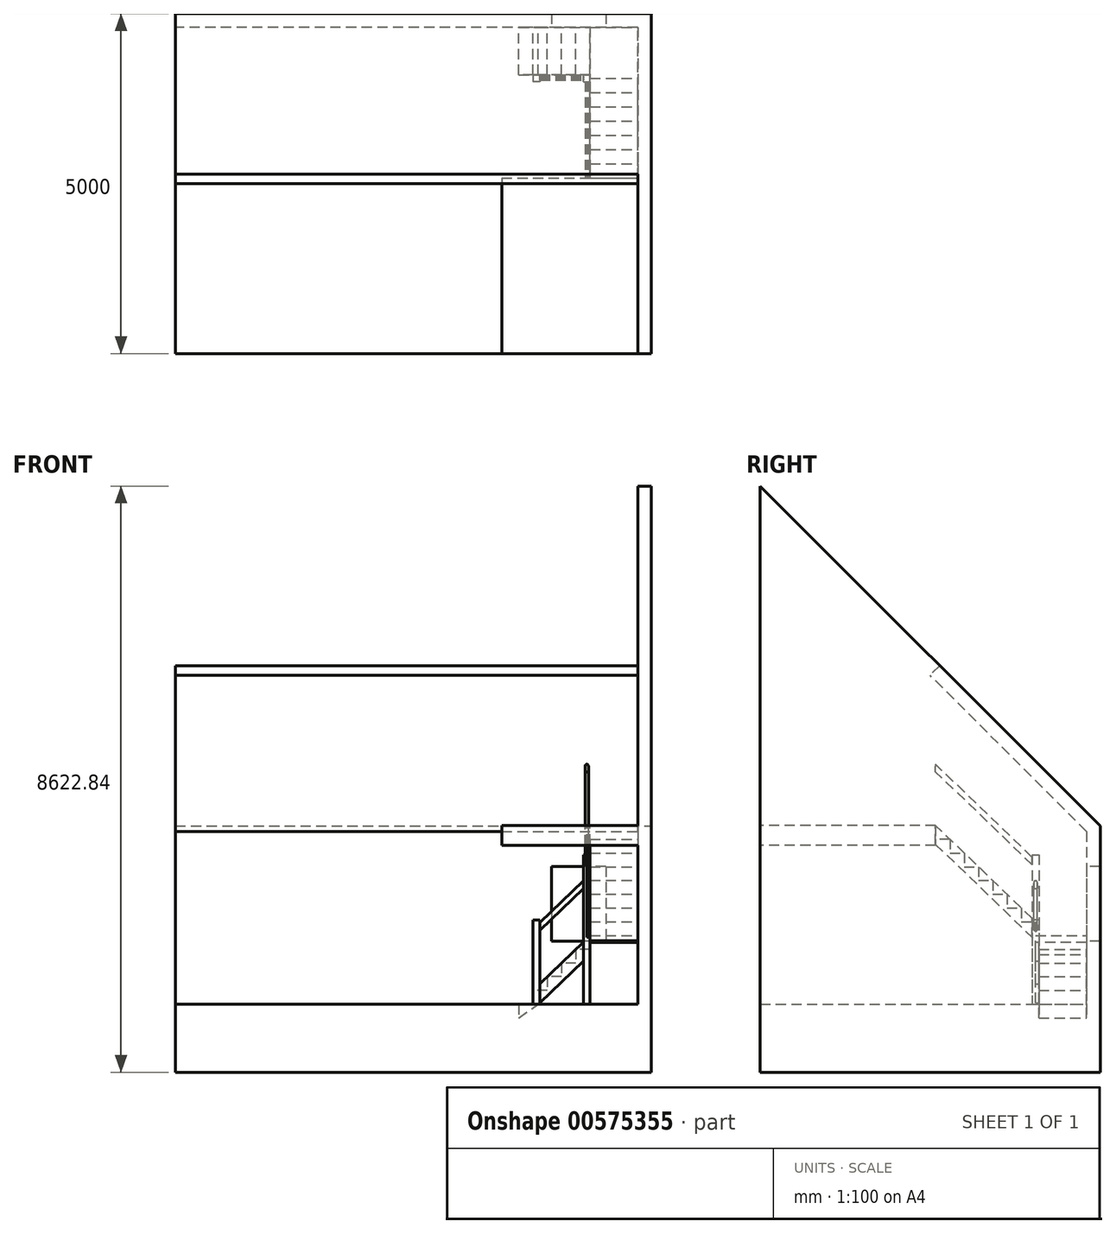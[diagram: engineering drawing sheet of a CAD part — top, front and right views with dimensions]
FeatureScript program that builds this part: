
annotation { "Feature Type Name" : "Feature", "Feature Type Description" : "" }
export const myFeature = defineFeature(function(context is Context, id is Id, definition is map)
    precondition{}
    {
        {
            var Q0;
            Q0=qCreatedBy(makeId("Top.planeOp"),FACE);
            var sketch = newSketch(context, id + "F0", { "sketchPlane" : qUnion([Q0])});
            skLineSegment(sketch, "E0.bottom", {"start": v(-3500, 2500) * mm, "end": v(3500, 2500) * mm});
            skLineSegment(sketch, "E0.top", {"start": v(-3500, -2500) * mm, "end": v(3500, -2500) * mm});
            skLineSegment(sketch, "E0.left", {"start": v(-3500, 2500) * mm, "end": v(-3500, -2500) * mm});
            skLineSegment(sketch, "E0.right", {"start": v(3500, 2500) * mm, "end": v(3500, -2500) * mm});
            skPoint(sketch, "E0.middle", {"position": v(0, 0) * mm});
            skSolve(sketch);
        }
        {
            var Q0;
            Q0=makeQuery(id+"F0.imprint","IMPRINT",FACE,{"disambiguationData":[TD([[makeQuery(id+"F0.imprint","IMPRINT",EDGE,{"derivedFrom":sQuery(id+"F0.wireOp",EDGE,"E0.bottom")}),-1.0]])]});
            extrude(context, id + "F1", {"entities" : qUnion([Q0]), "oppositeDirection" : true, "depth" : 1000 * mm, "offsetDistance" : 25 * mm});
        }
        {
            var Q0;
            Q0=makeQuery(id+"F1.opExtrude","CAP_FACE",FACE,{"disambiguationData":[OSD([sQuery(id+"F0.wireOp",EDGE,"E0.bottom"),sQuery(id+"F0.wireOp",EDGE,"E0.top"),sQuery(id+"F0.wireOp",EDGE,"E0.left"),sQuery(id+"F0.wireOp",EDGE,"E0.right")])],"isStart":true});
            var sketch = newSketch(context, id + "F2", { "sketchPlane" : qUnion([Q0])});
            skLineSegment(sketch, "E1", {"start": v(3500, 2500) * mm, "end": v(3500, -2500) * mm});
            skLineSegment(sketch, "E2", {"start": v(3500, -2500) * mm, "end": v(3300, -2500) * mm});
            skLineSegment(sketch, "E3", {"start": v(3300, -2500) * mm, "end": v(3300, 2300) * mm});
            skLineSegment(sketch, "E4", {"start": v(3300, 2300) * mm, "end": v(-3500, 2300) * mm});
            skLineSegment(sketch, "E5", {"start": v(-3500, 2300) * mm, "end": v(-3500, 2500) * mm});
            skLineSegment(sketch, "E6", {"start": v(-3500, 2500) * mm, "end": v(3500, 2500) * mm});
            skSolve(sketch);
        }
        {
            var Q0;
            Q0 = qSketchRegion(id + "F2", true);
            extrude(context, id + "F3", {"entities" : qUnion([Q0]), "operationType" : NewBodyOperationType.ADD, "depth" : 2300 * mm, "offsetDistance" : 25 * mm});
        }
        {
            var Q0;
            {var subQ1=sQuery(id+"F2.wireOp",EDGE,"E3");Q0=makeQuery(id+"F10.boolean.opBoolean","SPLIT",FACE,{"disambiguationData":[TD([makeQuery(id+"F10.opExtrude","SWEPT_FACE",FACE,{"disambiguationData":[OSD([sQuery(id+"F9.wireOp",EDGE,"E14")])]})])],"derivedFrom":makeQuery(id+"F3.opExtrude","SWEPT_FACE",FACE,{"disambiguationData":[OSD([subQ1])]})});}
            var sketch = newSketch(context, id + "F4", { "sketchPlane" : qUnion([Q0])});
            skLineSegment(sketch, "E7", {"start": v(-2300, 2540) * mm, "end": v(0, 4840) * mm});
            skLineSegment(sketch, "E8", {"start": v(-2300, 2300) * mm, "end": v(-2300, 2540) * mm});
            skLineSegment(sketch, "E9", {"start": v(-2300, 2300) * mm, "end": v(-2500, 2300) * mm});
            skLineSegment(sketch, "E10", {"start": v(-2500, 2300) * mm, "end": v(-2500, 2622.84) * mm});
            skLineSegment(sketch, "E11", {"start": v(-2500, 2622.84) * mm, "end": v(-141.42, 4981.42) * mm});
            skLineSegment(sketch, "E12", {"start": v(-141.42, 4981.42) * mm, "end": v(0, 4840) * mm});
            skSolve(sketch);
        }
        {
            var Q0;
            Q0 = qSketchRegion(id + "F4", true);
            var Q1;
            Q1=makeQuery(id+"F3.boolean.opBoolean","MERGE",FACE,{"derivedFrom":[makeQuery(id+"F1.opExtrude","SWEPT_FACE",FACE,{"disambiguationData":[OSD([sQuery(id+"F0.wireOp",EDGE,"E0.left")])]}),makeQuery(id+"F3.opExtrude","SWEPT_FACE",FACE,{"disambiguationData":[OSD([sQuery(id+"F2.wireOp",EDGE,"E5")])]})]});
            extrude(context, id + "F5", {"entities" : qUnion([Q0]), "operationType" : NewBodyOperationType.ADD, "endBound" : BoundingType.UP_TO_SURFACE, "depth" : 25 * mm, "endBoundEntityFace" : qUnion([Q1]), "offsetDistance" : 25 * mm});
        }
        {
            var Q0;
            Q0=makeQuery(id+"F3.opExtrude","CAP_FACE",FACE,{"disambiguationData":[OSD([sQuery(id+"F2.wireOp",EDGE,"E1"),sQuery(id+"F2.wireOp",EDGE,"E2"),sQuery(id+"F2.wireOp",EDGE,"E3"),sQuery(id+"F2.wireOp",EDGE,"E4"),sQuery(id+"F2.wireOp",EDGE,"E5"),sQuery(id+"F2.wireOp",EDGE,"E6")])],"isStart":false});
            var Q1;
            Q1=makeQuery(id+"F5.opExtrude","SWEPT_FACE",FACE,{"disambiguationData":[OSD([sQuery(id+"F4.wireOp",EDGE,"E11")])]});
            extrude(context, id + "F6", {"entities" : qUnion([Q0]), "operationType" : NewBodyOperationType.ADD, "endBound" : BoundingType.UP_TO_SURFACE, "depth" : 25 * mm, "endBoundEntityFace" : qUnion([Q1]), "offsetDistance" : 25 * mm});
        }
        {
            var Q0;
            {var subQ0=sQuery(id+"F2.wireOp",EDGE,"E3");Q0=makeQuery(id+"F6.boolean.opBoolean","MERGE",FACE,{"derivedFrom":[makeQuery(id+"F3.opExtrude","SWEPT_FACE",FACE,{"disambiguationData":[OSD([subQ0])]}),makeQuery(id+"F6.opExtrude","SWEPT_FACE",FACE,{"disambiguationData":[OSD([subQ0,sQuery(id+"F4.wireOp",EDGE,"E9")])]})]});}
            var sketch = newSketch(context, id + "F7", { "sketchPlane" : qUnion([Q0])});
            skLineSegment(sketch, "E13.bottom", {"start": v(-80, 2630) * mm, "end": v(2500, 2630) * mm});
            skLineSegment(sketch, "E13.top", {"start": v(-80, 2340) * mm, "end": v(2500, 2340) * mm});
            skLineSegment(sketch, "E13.left", {"start": v(-80, 2630) * mm, "end": v(-80, 2340) * mm});
            skLineSegment(sketch, "E13.right", {"start": v(2500, 2630) * mm, "end": v(2500, 2340) * mm});
            skSolve(sketch);
        }
        {
            var Q0;
            Q0=makeQuery(id+"F7.imprint","IMPRINT",FACE,{"disambiguationData":[TD([[makeQuery(id+"F7.imprint","IMPRINT",EDGE,{"derivedFrom":sQuery(id+"F7.wireOp",EDGE,"E13.bottom")}),-1.0]])]});
            extrude(context, id + "F8", {"entities" : qUnion([Q0]), "operationType" : NewBodyOperationType.ADD, "depth" : 2000 * mm, "offsetDistance" : 25 * mm});
        }
        {
            var Q0;
            Q0=makeQuery(id+"F3.opExtrude","SWEPT_FACE",FACE,{"disambiguationData":[OSD([sQuery(id+"F2.wireOp",EDGE,"E3")])]});
            var sketch = newSketch(context, id + "F9", { "sketchPlane" : qUnion([Q0])});
            skLineSegment(sketch, "E14", {"start": v(-290, 2427.7) * mm, "end": v(-290, 2225.4) * mm});
            skLineSegment(sketch, "E15", {"start": v(-290, 2225.4) * mm, "end": v(-500, 2225.4) * mm});
            skLineSegment(sketch, "E16", {"start": v(-500, 2225.4) * mm, "end": v(-500, 2023.1) * mm});
            skLineSegment(sketch, "E17", {"start": v(-500, 2023.1) * mm, "end": v(-710, 2023.1) * mm});
            skLineSegment(sketch, "E18", {"start": v(-710, 2023.1) * mm, "end": v(-710, 1820.8) * mm});
            skLineSegment(sketch, "E19", {"start": v(-710, 1820.8) * mm, "end": v(-920, 1820.8) * mm});
            skLineSegment(sketch, "E20", {"start": v(-920, 1820.8) * mm, "end": v(-920, 1618.5) * mm});
            skLineSegment(sketch, "E21", {"start": v(-920, 1618.5) * mm, "end": v(-1130, 1618.5) * mm});
            skLineSegment(sketch, "E22", {"start": v(-1130, 1618.5) * mm, "end": v(-1130, 1416.2) * mm});
            skLineSegment(sketch, "E23", {"start": v(-1130, 1416.2) * mm, "end": v(-1340, 1416.2) * mm});
            skLineSegment(sketch, "E24", {"start": v(-1550, 1011.6) * mm, "end": v(-2300, 1011.6) * mm});
            skLineSegment(sketch, "E25", {"start": v(-2300, 1011.6) * mm, "end": v(-2300, 911.6) * mm});
            skLineSegment(sketch, "E26", {"start": v(-2300, 911.6) * mm, "end": v(-1550, 911.6) * mm});
            skLineSegment(sketch, "E27", {"start": v(-290, 2427.7) * mm, "end": v(-1760, 1011.6) * mm, "construction": true});
            skLineSegment(sketch, "E28", {"start": v(-1550, 1011.6) * mm, "end": v(-1550, 911.6) * mm, "construction": true});
            skLineSegment(sketch, "E29", {"start": v(-80, 2352.3) * mm, "end": v(-1550, 936.2) * mm});
            skLineSegment(sketch, "E30", {"start": v(-1550, 911.6) * mm, "end": v(-1550, 936.2) * mm});
            skLineSegment(sketch, "E31", {"start": v(-290, 2427.7) * mm, "end": v(-80, 2427.7) * mm});
            skLineSegment(sketch, "E32", {"start": v(-80, 2427.7) * mm, "end": v(-80, 2352.3) * mm});
            skLineSegment(sketch, "E33", {"start": v(-1340, 1416.2) * mm, "end": v(-1340, 1213.9) * mm});
            skLineSegment(sketch, "E34", {"start": v(-1340, 1213.9) * mm, "end": v(-1550, 1213.9) * mm});
            skLineSegment(sketch, "E35", {"start": v(-1550, 1213.9) * mm, "end": v(-1550, 1011.6) * mm});
            skSolve(sketch);
        }
        {
            var Q0;
            Q0 = qSketchRegion(id + "F9", true);
            extrude(context, id + "F10", {"entities" : qUnion([Q0]), "depth" : 700 * mm, "offsetDistance" : 25 * mm});
        }
        {
            var Q0;
            Q0=makeQuery(id+"F3.opExtrude","SWEPT_FACE",FACE,{"disambiguationData":[OSD([sQuery(id+"F2.wireOp",EDGE,"E4")])]});
            var sketch = newSketch(context, id + "F11", { "sketchPlane" : qUnion([Q0])});
            skLineSegment(sketch, "E36", {"start": v(2600, 809.3) * mm, "end": v(2390, 809.3) * mm});
            skLineSegment(sketch, "E37", {"start": v(2390, 809.3) * mm, "end": v(2390, 607) * mm});
            skLineSegment(sketch, "E38", {"start": v(2390, 607) * mm, "end": v(2180, 607) * mm});
            skLineSegment(sketch, "E39", {"start": v(2180, 607) * mm, "end": v(2180, 404.7) * mm});
            skLineSegment(sketch, "E40", {"start": v(2180, 404.7) * mm, "end": v(1970, 404.7) * mm});
            skLineSegment(sketch, "E41", {"start": v(1838.17, 0) * mm, "end": v(2600, 733.9) * mm});
            skLineSegment(sketch, "E42", {"start": v(2600, 733.9) * mm, "end": v(2600, 809.3) * mm});
            skLineSegment(sketch, "E43", {"start": v(1970, 404.7) * mm, "end": v(2180, 607) * mm, "construction": true});
            skLineSegment(sketch, "E44", {"start": v(1970, 404.7) * mm, "end": v(1970, 202.4) * mm});
            skLineSegment(sketch, "E45", {"start": v(1970, 202.4) * mm, "end": v(1760, 202.4) * mm});
            skLineSegment(sketch, "E46", {"start": v(1760, 202.4) * mm, "end": v(1760, 0.1) * mm});
            skLineSegment(sketch, "E47", {"start": v(2600, 809.3) * mm, "end": v(2600, 911.6) * mm, "construction": true});
            skLineSegment(sketch, "E48", {"start": v(1760, 0.1) * mm, "end": v(1550, 0.1) * mm});
            skLineSegment(sketch, "E49", {"start": v(1550, 0.1) * mm, "end": v(1550, -202.2) * mm});
            skLineSegment(sketch, "E50", {"start": v(1550, -202.2) * mm, "end": v(1838.17, 0) * mm});
            skSolve(sketch);
        }
        {
            var Q0;
            Q0 = qSketchRegion(id + "F11", true);
            extrude(context, id + "F12", {"entities" : qUnion([Q0]), "depth" : 700 * mm, "offsetDistance" : 25 * mm});
        }
        {
            var Q0;
            Q0=makeQuery(id+"F5.boolean.opBoolean","MERGE",FACE,{"derivedFrom":[makeQuery(id+"F3.opExtrude","SWEPT_FACE",FACE,{"disambiguationData":[OSD([sQuery(id+"F2.wireOp",EDGE,"E4")])]}),makeQuery(id+"F5.opExtrude","SWEPT_FACE",FACE,{"disambiguationData":[OSD([sQuery(id+"F4.wireOp",EDGE,"E8")])]})]});
            var sketch = newSketch(context, id + "F13", { "sketchPlane" : qUnion([Q0])});
            skLineSegment(sketch, "E51.bottom", {"start": v(2830, 2025) * mm, "end": v(2030, 2025) * mm});
            skLineSegment(sketch, "E51.top", {"start": v(2830, 925) * mm, "end": v(2030, 925) * mm});
            skLineSegment(sketch, "E51.left", {"start": v(2830, 2025) * mm, "end": v(2830, 925) * mm});
            skLineSegment(sketch, "E51.right", {"start": v(2030, 2025) * mm, "end": v(2030, 925) * mm});
            skPoint(sketch, "E51.middle", {"position": v(2430, 1475) * mm});
            skSolve(sketch);
        }
        {
            var Q0;
            Q0=makeQuery(id+"F13.imprint","IMPRINT",FACE,{"disambiguationData":[TD([[makeQuery(id+"F13.imprint","IMPRINT",EDGE,{"derivedFrom":sQuery(id+"F13.wireOp",EDGE,"E51.bottom")}),1.0]])]});
            extrude(context, id + "F14", {"entities" : qUnion([Q0]), "operationType" : NewBodyOperationType.REMOVE, "endBound" : BoundingType.THROUGH_ALL, "oppositeDirection" : true, "depth" : 25 * mm, "offsetDistance" : 25 * mm});
        }
        {
            var Q0;
            Q0=makeQuery(id+"F1.opExtrude","CAP_FACE",FACE,{"disambiguationData":[OSD([sQuery(id+"F0.wireOp",EDGE,"E0.bottom"),sQuery(id+"F0.wireOp",EDGE,"E0.top"),sQuery(id+"F0.wireOp",EDGE,"E0.left"),sQuery(id+"F0.wireOp",EDGE,"E0.right")])],"isStart":true});
            var sketch = newSketch(context, id + "F15", { "sketchPlane" : qUnion([Q0])});
            skLineSegment(sketch, "E52.bottom", {"start": v(2500, 1500) * mm, "end": v(2600, 1500) * mm});
            skLineSegment(sketch, "E52.top", {"start": v(2500, 1600) * mm, "end": v(2600, 1600) * mm});
            skLineSegment(sketch, "E52.left", {"start": v(2500, 1500) * mm, "end": v(2500, 1600) * mm});
            skLineSegment(sketch, "E52.right", {"start": v(2600, 1500) * mm, "end": v(2600, 1600) * mm});
            skPoint(sketch, "E52.middle", {"position": v(2550, 1550) * mm});
            skSolve(sketch);
        }
        {
            var Q0;
            Q0=makeQuery(id+"F15.imprint","IMPRINT",FACE,{"disambiguationData":[TD([[makeQuery(id+"F15.imprint","IMPRINT",EDGE,{"derivedFrom":sQuery(id+"F15.wireOp",EDGE,"E52.bottom")}),1.0]])]});
            extrude(context, id + "F16", {"entities" : qUnion([Q0]), "depth" : 2200 * mm, "offsetDistance" : 25 * mm});
        }
        {
            var Q0;
            Q0=makeQuery(id+"F10.opExtrude","CAP_FACE",FACE,{"disambiguationData":[OSD([sQuery(id+"F9.wireOp",EDGE,"E14"),sQuery(id+"F9.wireOp",EDGE,"E15"),sQuery(id+"F9.wireOp",EDGE,"E16"),sQuery(id+"F9.wireOp",EDGE,"E17"),sQuery(id+"F9.wireOp",EDGE,"E18"),sQuery(id+"F9.wireOp",EDGE,"E19"),sQuery(id+"F9.wireOp",EDGE,"E20"),sQuery(id+"F9.wireOp",EDGE,"E21"),sQuery(id+"F9.wireOp",EDGE,"E22"),sQuery(id+"F9.wireOp",EDGE,"E23"),sQuery(id+"F9.wireOp",EDGE,"E24"),sQuery(id+"F9.wireOp",EDGE,"E25"),sQuery(id+"F9.wireOp",EDGE,"E26"),sQuery(id+"F9.wireOp",EDGE,"E29"),sQuery(id+"F9.wireOp",EDGE,"E30"),sQuery(id+"F9.wireOp",EDGE,"E31"),sQuery(id+"F9.wireOp",EDGE,"E32"),sQuery(id+"F9.wireOp",EDGE,"E33"),sQuery(id+"F9.wireOp",EDGE,"E34"),sQuery(id+"F9.wireOp",EDGE,"E35")])],"isStart":false});
            var sketch = newSketch(context, id + "F17", { "sketchPlane" : qUnion([Q0])});
            skLineSegment(sketch, "E53", {"start": v(-1500, 2162.07) * mm, "end": v(-80, 3530) * mm});
            skLineSegment(sketch, "E54", {"start": v(-80, 2427.7) * mm, "end": v(-80, 3530) * mm, "construction": true});
            skLineSegment(sketch, "E55", {"start": v(-710, 2023.1) * mm, "end": v(-710, 2923.1) * mm, "construction": true});
            skLineSegment(sketch, "E56", {"start": v(-80, 3530) * mm, "end": v(-426.9, 3890.1) * mm, "construction": true});
            skLineSegment(sketch, "E57.0", {"start": v(-1500, 2050.98) * mm, "end": v(-80, 3418.92) * mm});
            skLineSegment(sketch, "E58", {"start": v(-1500, 2050.98) * mm, "end": v(-1500, 2162.07) * mm});
            skLineSegment(sketch, "E59", {"start": v(-80, 3418.92) * mm, "end": v(-80, 3530) * mm});
            skSolve(sketch);
        }
        {
            var Q0;
            Q0=makeQuery(id+"F17.imprint","IMPRINT",FACE,{"disambiguationData":[TD([[makeQuery(id+"F17.imprint","IMPRINT",EDGE,{"derivedFrom":sQuery(id+"F17.wireOp",EDGE,"E53")}),-1.0]])]});
            extrude(context, id + "F18", {"entities" : qUnion([Q0]), "operationType" : NewBodyOperationType.ADD, "depth" : 75 * mm, "offsetDistance" : 25 * mm, "hasSecondDirection" : true, "secondDirectionOppositeDirection" : true, "secondDirectionDepth" : -25 * mm});
        }
        {
            var Q0;
            Q0=makeQuery(id+"F16.opExtrude","CAP_FACE",FACE,{"disambiguationData":[OSD([sQuery(id+"F15.wireOp",EDGE,"E52.bottom"),sQuery(id+"F15.wireOp",EDGE,"E52.top"),sQuery(id+"F15.wireOp",EDGE,"E52.left"),sQuery(id+"F15.wireOp",EDGE,"E52.right")])],"isStart":true});
            var sketch = newSketch(context, id + "F19", { "sketchPlane" : qUnion([Q0])});
            skLineSegment(sketch, "E60.bottom", {"start": v(1860, -1600) * mm, "end": v(1760, -1600) * mm});
            skLineSegment(sketch, "E60.top", {"start": v(1860, -1500) * mm, "end": v(1760, -1500) * mm});
            skLineSegment(sketch, "E60.left", {"start": v(1860, -1600) * mm, "end": v(1860, -1500) * mm});
            skLineSegment(sketch, "E60.right", {"start": v(1760, -1600) * mm, "end": v(1760, -1500) * mm});
            skPoint(sketch, "E60.middle", {"position": v(1810, -1550) * mm});
            skSolve(sketch);
        }
        {
            var Q0;
            Q0=makeQuery(id+"F19.imprint","IMPRINT",FACE,{"disambiguationData":[TD([[makeQuery(id+"F19.imprint","IMPRINT",EDGE,{"derivedFrom":sQuery(id+"F19.wireOp",EDGE,"E60.bottom")}),-1.0]])]});
            extrude(context, id + "F20", {"entities" : qUnion([Q0]), "oppositeDirection" : true, "depth" : 1236 * mm, "offsetDistance" : 25 * mm});
        }
        {
            var Q0;
            Q0=makeQuery(id+"F12.opExtrude","CAP_FACE",FACE,{"disambiguationData":[OSD([sQuery(id+"F11.wireOp",EDGE,"E36"),sQuery(id+"F11.wireOp",EDGE,"E37"),sQuery(id+"F11.wireOp",EDGE,"E38"),sQuery(id+"F11.wireOp",EDGE,"E39"),sQuery(id+"F11.wireOp",EDGE,"E40"),sQuery(id+"F11.wireOp",EDGE,"E41"),sQuery(id+"F11.wireOp",EDGE,"E42"),sQuery(id+"F11.wireOp",EDGE,"E44"),sQuery(id+"F11.wireOp",EDGE,"E45"),sQuery(id+"F11.wireOp",EDGE,"E46"),sQuery(id+"F11.wireOp",EDGE,"E48"),sQuery(id+"F11.wireOp",EDGE,"E49"),sQuery(id+"F11.wireOp",EDGE,"E50")])],"isStart":false});
            var sketch = newSketch(context, id + "F21", { "sketchPlane" : qUnion([Q0])});
            skLineSegment(sketch, "E61", {"start": v(1860, 1198.73) * mm, "end": v(2500, 1815.27) * mm});
            skLineSegment(sketch, "E62", {"start": v(1970, 404.7) * mm, "end": v(1970, 1304.7) * mm, "construction": true});
            skLineSegment(sketch, "E63", {"start": v(1860, 1087.65) * mm, "end": v(2500, 1704.18) * mm});
            skLineSegment(sketch, "E64", {"start": v(1860, 1198.73) * mm, "end": v(1860, 1087.65) * mm});
            skLineSegment(sketch, "E65", {"start": v(2500, 1815.27) * mm, "end": v(2500, 1704.18) * mm});
            skSolve(sketch);
        }
        {
            var Q0;
            Q0=makeQuery(id+"F21.imprint","IMPRINT",FACE,{"disambiguationData":[TD([[makeQuery(id+"F21.imprint","IMPRINT",EDGE,{"derivedFrom":makeQuery(id+"F12.opExtrude","CAP_EDGE",EDGE,{"disambiguationData":[OSD([sQuery(id+"F11.wireOp",EDGE,"E36")])],"isStart":false})}),1.0]])]});
            var sketch = newSketch(context, id + "F22", { "sketchPlane" : qUnion([Q0])});
            skLineSegment(sketch, "E66", {"start": v(1860, 21.03) * mm, "end": v(2500, 637.56) * mm});
            skLineSegment(sketch, "E67.0", {"start": v(1860, 298.73) * mm, "end": v(2500, 915.27) * mm});
            skLineSegment(sketch, "E68", {"start": v(1860, 21.03) * mm, "end": v(1860, 298.73) * mm});
            skLineSegment(sketch, "E69", {"start": v(2500, 637.56) * mm, "end": v(2500, 915.27) * mm});
            skSolve(sketch);
        }
        {
            var Q0;
            {var subQ1=makeQuery(id+"F21.imprint","IMPRINT",EDGE,{"derivedFrom":makeQuery(id+"F12.opExtrude","CAP_EDGE",EDGE,{"disambiguationData":[OSD([sQuery(id+"F11.wireOp",EDGE,"E37")])],"isStart":false})});Q0=makeQuery(id+"F22.imprint","IMPRINT",FACE,{"disambiguationData":[TD([[makeQuery(id+"F22.imprint","IMPRINT",EDGE,{"derivedFrom":subQ1}),-1.0]])]});}
            var Q1;
            {var subQ4=sQuery(id+"F22.wireOp",EDGE,"E66");Q1=makeQuery(id+"F22.imprint","IMPRINT",FACE,{"disambiguationData":[TD([[makeQuery(id+"F22.imprint","IMPRINT",EDGE,{"derivedFrom":subQ4}),1.0]])]});}
            var Q2;
            {var subQ1=makeQuery(id+"F21.imprint","IMPRINT",EDGE,{"derivedFrom":makeQuery(id+"F12.opExtrude","CAP_EDGE",EDGE,{"disambiguationData":[OSD([sQuery(id+"F11.wireOp",EDGE,"E39")])],"isStart":false})});Q2=makeQuery(id+"F22.imprint","IMPRINT",FACE,{"disambiguationData":[TD([[makeQuery(id+"F22.imprint","IMPRINT",EDGE,{"derivedFrom":subQ1}),-1.0]])]});}
            var Q3;
            {var subQ1=makeQuery(id+"F21.imprint","IMPRINT",EDGE,{"derivedFrom":makeQuery(id+"F12.opExtrude","CAP_EDGE",EDGE,{"disambiguationData":[OSD([sQuery(id+"F11.wireOp",EDGE,"E44")])],"isStart":false})});Q3=makeQuery(id+"F22.imprint","IMPRINT",FACE,{"disambiguationData":[TD([[makeQuery(id+"F22.imprint","IMPRINT",EDGE,{"derivedFrom":subQ1}),-1.0]])]});}
            var Q4;
            {var subQ0=sQuery(id+"F22.wireOp",EDGE,"E67.0");var subQ3=sQuery(id+"F22.wireOp",EDGE,"E69");var subQ4=makeQuery(id+"F22.imprint","INTERSECT",VERTEX,{"derivedFrom":[subQ0,subQ3]});Q4=makeQuery(id+"F22.imprint","IMPRINT",FACE,{"disambiguationData":[TD([[makeQuery(id+"F22.imprint","IMPRINT",EDGE,{"disambiguationData":[TD([[subQ4,1.0]])],"derivedFrom":subQ3}),1.0]])]});}
            extrude(context, id + "F23", {"entities" : qUnion([Q0, Q1, Q2, Q3, Q4]), "depth" : 50 * mm, "offsetDistance" : 25 * mm});
        }
        {
            var Q0;
            Q0=makeQuery(id+"F10.opExtrude","CAP_FACE",FACE,{"disambiguationData":[OSD([sQuery(id+"F9.wireOp",EDGE,"E14"),sQuery(id+"F9.wireOp",EDGE,"E15"),sQuery(id+"F9.wireOp",EDGE,"E16"),sQuery(id+"F9.wireOp",EDGE,"E17"),sQuery(id+"F9.wireOp",EDGE,"E18"),sQuery(id+"F9.wireOp",EDGE,"E19"),sQuery(id+"F9.wireOp",EDGE,"E20"),sQuery(id+"F9.wireOp",EDGE,"E21"),sQuery(id+"F9.wireOp",EDGE,"E22"),sQuery(id+"F9.wireOp",EDGE,"E23"),sQuery(id+"F9.wireOp",EDGE,"E24"),sQuery(id+"F9.wireOp",EDGE,"E25"),sQuery(id+"F9.wireOp",EDGE,"E26"),sQuery(id+"F9.wireOp",EDGE,"E29"),sQuery(id+"F9.wireOp",EDGE,"E30"),sQuery(id+"F9.wireOp",EDGE,"E31"),sQuery(id+"F9.wireOp",EDGE,"E32"),sQuery(id+"F9.wireOp",EDGE,"E33"),sQuery(id+"F9.wireOp",EDGE,"E34"),sQuery(id+"F9.wireOp",EDGE,"E35")])],"isStart":false});
            var sketch = newSketch(context, id + "F24", { "sketchPlane" : qUnion([Q0])});
            skLineSegment(sketch, "E70", {"start": v(-1500, 984.36) * mm, "end": v(-80, 2352.3) * mm});
            skLineSegment(sketch, "E71", {"start": v(-1500, 1262.07) * mm, "end": v(-80, 2630) * mm});
            skLineSegment(sketch, "E72", {"start": v(-1500, 984.36) * mm, "end": v(-1500, 1262.07) * mm});
            skLineSegment(sketch, "E73", {"start": v(-80, 2352.3) * mm, "end": v(-80, 2630) * mm});
            skSolve(sketch);
        }
        {
            var Q0;
            Q0 = qSketchRegion(id + "F24", true);
            extrude(context, id + "F25", {"entities" : qUnion([Q0]), "depth" : 50 * mm, "offsetDistance" : 25 * mm});
        }
        {
            var Q0;
            Q0 = qSketchRegion(id + "F21", true);
            extrude(context, id + "F26", {"entities" : qUnion([Q0]), "depth" : 75 * mm, "offsetDistance" : 25 * mm, "hasSecondDirection" : true, "secondDirectionOppositeDirection" : true, "secondDirectionDepth" : -25 * mm});
        }
        {
            var Q0;
            Q0=makeQuery(id+"F18.opExtrude","CAP_EDGE",EDGE,{"disambiguationData":[OSD([sQuery(id+"F17.wireOp",EDGE,"E53")])],"isStart":false});
            var Q1;
            Q1=makeQuery(id+"F18.opExtrude","CAP_EDGE",EDGE,{"disambiguationData":[OSD([sQuery(id+"F17.wireOp",EDGE,"E53")])],"isStart":true});
            var Q2;
            Q2=makeQuery(id+"F26.opExtrude","CAP_EDGE",EDGE,{"disambiguationData":[OSD([sQuery(id+"F21.wireOp",EDGE,"E61")])],"isStart":true});
            var Q3;
            Q3=makeQuery(id+"F26.opExtrude","CAP_EDGE",EDGE,{"disambiguationData":[OSD([sQuery(id+"F21.wireOp",EDGE,"E61")])],"isStart":false});
            fillet(context, id + "F27", {"entities" : qUnion([Q0, Q1, Q2, Q3]), "radius" : 20 * mm, "tangentPropagation" : true, "allowEdgeOverflow" : false});
        }
    });
